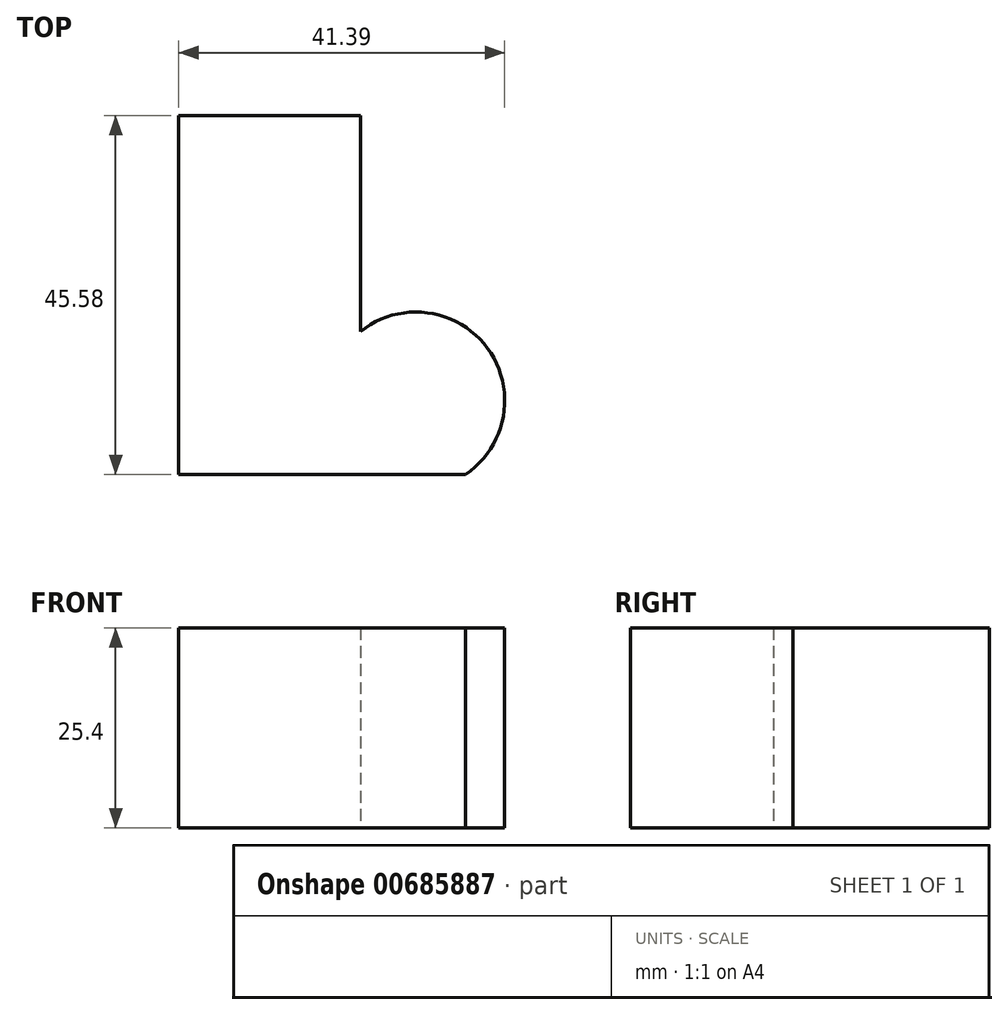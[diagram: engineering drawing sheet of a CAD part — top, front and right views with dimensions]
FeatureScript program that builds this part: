
annotation { "Feature Type Name" : "Feature", "Feature Type Description" : "" }
export const myFeature = defineFeature(function(context is Context, id is Id, definition is map)
    precondition{}
    {
        {
            var Q0;
            Q0=qCreatedBy(makeId("Top.planeOp"),FACE);
            var sketch = newSketch(context, id + "F0", { "sketchPlane" : qUnion([Q0])});
            skLineSegment(sketch, "E0", {"start": v(0, 0) * mm, "end": v(-36.4, 0) * mm});
            skLineSegment(sketch, "E1", {"start": v(-36.4, 0) * mm, "end": v(-36.4, 45.58) * mm});
            skLineSegment(sketch, "E2", {"start": v(-36.4, 45.58) * mm, "end": v(-13.32, 45.58) * mm});
            skLineSegment(sketch, "E3", {"start": v(-13.32, 45.58) * mm, "end": v(-13.32, 18.15) * mm});
            skArc(sketch, "E4", {"start": v(0, 0) * mm, "mid": v(2.81, 16.02) * mm, "end": v(-13.32, 18.15) * mm});
            skSolve(sketch);
        }
        {
            var Q0;
            Q0 = qSketchRegion(id + "F0", true);
            extrude(context, id + "F1", {"entities" : qUnion([Q0]), "depth" : 25.4 * mm, "offsetDistance" : 25.4 * mm});
        }
    });
